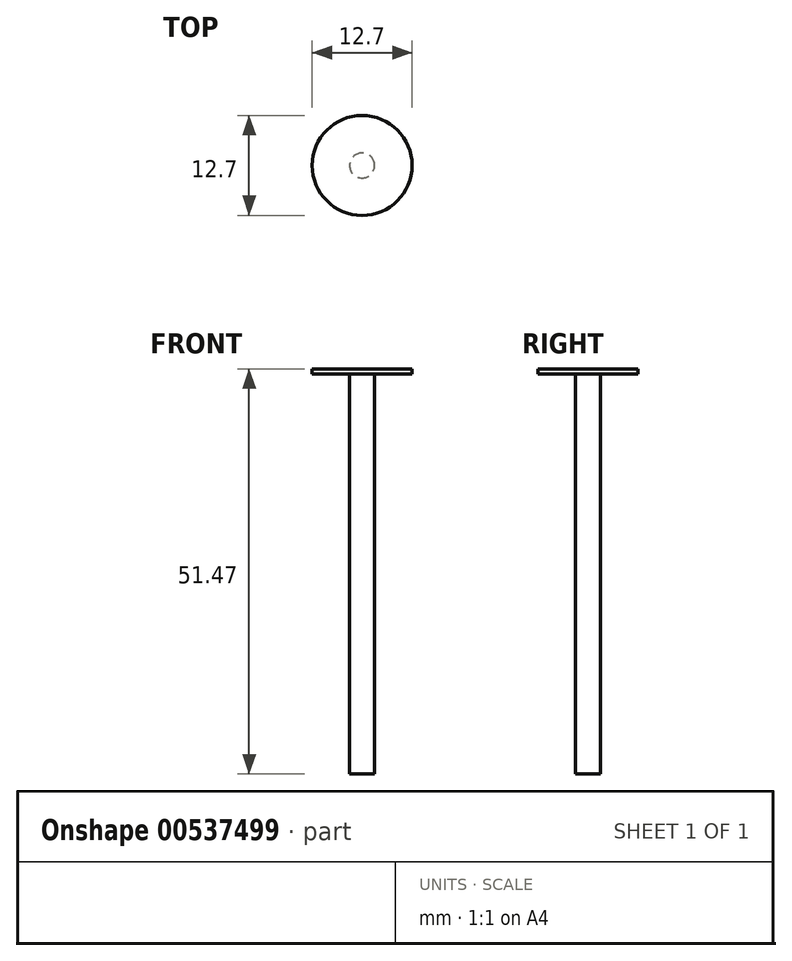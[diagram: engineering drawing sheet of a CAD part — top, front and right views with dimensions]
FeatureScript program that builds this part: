
annotation { "Feature Type Name" : "Feature", "Feature Type Description" : "" }
export const myFeature = defineFeature(function(context is Context, id is Id, definition is map)
    precondition{}
    {
        {
            var Q0;
            Q0=qCreatedBy(makeId("Top.planeOp"),FACE);
            var sketch = newSketch(context, id + "F0", { "sketchPlane" : qUnion([Q0])});
            skCircle(sketch, "E0", {"center": v(0, 0) * mm, "radius": 1.59 * mm});
            skSolve(sketch);
        }
        {
            var Q0;
            Q0=makeQuery(id+"F0.imprint","IMPRINT",FACE,{"disambiguationData":[TD([[makeQuery(id+"F0.imprint","IMPRINT",EDGE,{"derivedFrom":sQuery(id+"F0.wireOp",EDGE,"E0")}),1.0]])]});
            var Q1;
            Q1=sQuery(id+"F0.wireOp",EDGE,"E0");
            extrude(context, id + "F1", {"entities" : qUnion([Q0]), "surfaceEntities" : qUnion([Q1]), "oppositeDirection" : true, "depth" : 50.8 * mm, "offsetDistance" : 25.4 * mm});
        }
        {
            var Q0;
            Q0=makeQuery(id+"F1.opExtrude","CAP_FACE",FACE,{"disambiguationData":[OSD([sQuery(id+"F0.wireOp",EDGE,"E0")])],"isStart":true});
            var sketch = newSketch(context, id + "F2", { "sketchPlane" : qUnion([Q0])});
            skCircle(sketch, "E1", {"center": v(0, 0) * mm, "radius": 6.35 * mm});
            skSolve(sketch);
        }
        {
            var Q0;
            Q0 = qSketchRegion(id + "F2", true);
            extrude(context, id + "F3", {"entities" : qUnion([Q0]), "operationType" : NewBodyOperationType.ADD, "depth" : 0.67 * mm, "offsetDistance" : 25.4 * mm});
        }
    });
